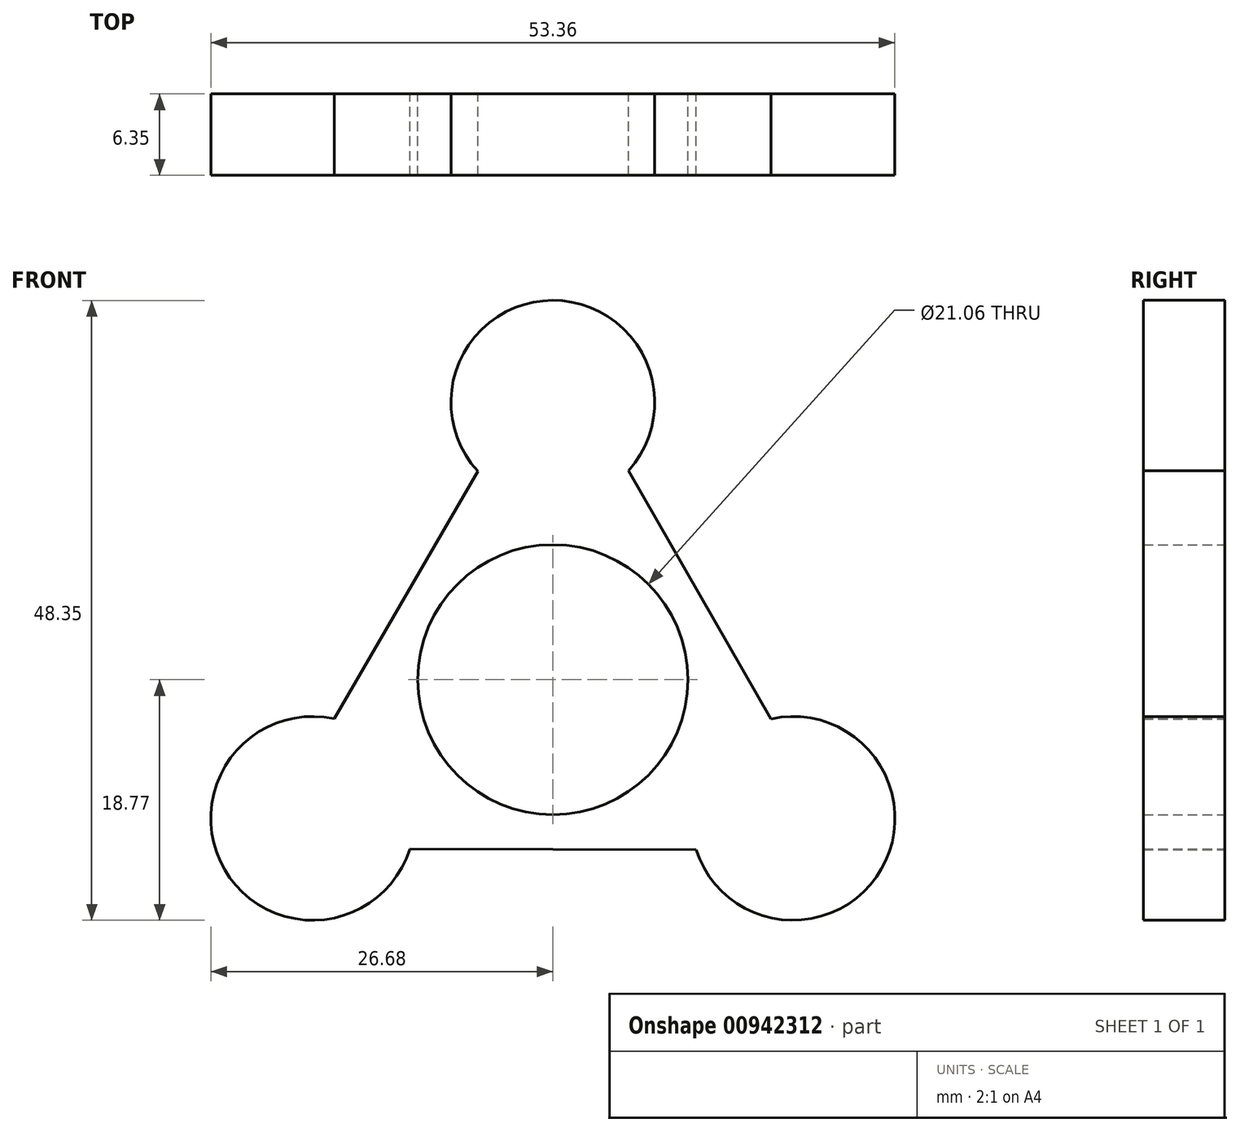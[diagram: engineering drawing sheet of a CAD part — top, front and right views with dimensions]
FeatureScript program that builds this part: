
annotation { "Feature Type Name" : "Feature", "Feature Type Description" : "" }
export const myFeature = defineFeature(function(context is Context, id is Id, definition is map)
    precondition{}
    {
        {
            var Q0;
            Q0=qCreatedBy(makeId("Front.planeOp"),FACE);
            var sketch = newSketch(context, id + "F0", { "sketchPlane" : qUnion([Q0])});
            skCircle(sketch, "E0", {"center": v(0, 0) * mm, "radius": 5.59 * mm});
            skCircle(sketch, "E1", {"center": v(0, 0) * mm, "radius": 10.53 * mm});
            skCircle(sketch, "E2", {"center": v(0, 21.63) * mm, "radius": 7.95 * mm});
            skCircle(sketch, "E3.1.0", {"center": v(-18.74, -10.82) * mm, "radius": 7.95 * mm});
            skCircle(sketch, "E3.2.0", {"center": v(18.74, -10.82) * mm, "radius": 7.95 * mm});
            skLineSegment(sketch, "E4", {"start": v(-5.86, 16.26) * mm, "end": v(-17.06, -3.05) * mm});
            skLineSegment(sketch, "E5.1.0", {"start": v(-11.15, -13.2) * mm, "end": v(11.17, -13.25) * mm});
            skLineSegment(sketch, "E5.2.0", {"start": v(17.01, -3.06) * mm, "end": v(5.9, 16.3) * mm});
            skSolve(sketch);
        }
        {
            var Q0;
            Q0 = qSketchRegion(id + "F0", true);
            extrude(context, id + "F1", {"entities" : qUnion([Q0]), "depth" : 6.35 * mm, "offsetDistance" : 25.4 * mm});
        }
    });
